# Revit family: Reece_Toilet_American Standard_Cygnet_Close Coupled Back to Wall_Bottom Inlet_With E Bidet
name_source: partatom
category: Plumbing Fixtures
revit_build: Autodesk Revit 2018 (Build: 20190510_1515(x64)
units: mm (PartAtom-declared; Revit-internal decimal feet)

## family parameters
Always vertical = Yes
Cut with Voids When Loaded = Yes
Part Type = Normal
Room Calculation Point = No
Round Connector Dimension = Use Diameter
Shared = No
Work Plane-Based = Yes

## types (1)
- Round_Soft Close_White
    Default Elevation = 0 mm  [stored 0 ft]
    Description = American Standard Cygnet Round Hygiene Rim Close Coupled Back to Wall Bottom Inlet Toilet Suite with SpaLet E-Bidet Seat White (4 Star)
    Disclaimer = THIS FILE IS THE PROPERTY OF THE REECE GROUP. IT MAY NOT BE REPRODUCED, REVERSE-ENGINEERED OR MODIFIED. ANY REPUBLICATION, TRANSMISSION OR DISTRIBUTION FOR THE PURPOSE OF COMMERCIALLY EXPLOITING THE FILES IS PROHIBITED.
    Keynote = Product #1805208, Reece_Toilet_American Standard_Cygnet_Close Coupled Back to Wall_Bottom Inlet_With E Bidet - Round_Soft Close_White
    Manufacturer = American Standard
    Model = Cygnet
    Reece_Back_Outlet_Offset = 190 mm  [stored 0.62336 ft]
    Reece_Bottom_Inlet = 12 mm  [stored 0.0393701 ft]
    Reece_Bottom_Outlet_Offset = 140 mm  [stored 0.459318 ft]
    Reece_Cistern = Reece_Toilet_American Standard_Cygnet_SpaLet_Round_Bottom Inlet_Cistern_Nested
    Reece_Cistern_Width = 375 mm  [stored 1.23031 ft]
    Reece_Detail_Additional = Close Coupled Back to Wall
    Reece_Detail_Connector = Bottom Inlet
    Reece_Detail_Disclaimer = THIS FILE IS THE PROPERTY OF THE REECE GROUP. IT MAY NOT BE REPRODUCED, REVERSE-ENGINEERED OR MODIFIED. ANY REPUBLICATION, TRANSMISSION OR DISTRIBUTION FOR THE PURPOSE OF COMMERCIALLY EXPLOITING THE FILES IS PROHIBITED.
    Reece_Detail_Function = P Trap / S Trap using conversion bend (supplied)
    Reece_Detail_Installation = Electrical input required. Refer to web page for further details.
    Reece_Detail_Shape = Round
    Reece_E Bidet_Inlet = 12 mm  [stored 0.0393701 ft]
    Reece_Material_Cistern = Reece_Vitreous China_White
    Reece_Material_Colour = Reece_Brass_Chrome
    Reece_Material_Main = Reece_Vitreous China_White
    Reece_Material_Seat = Reece_Plastic_White
    Reece_Material_Secondary = Reece_Brass_Chrome
    Reece_Overall_Height = 807 mm
    Reece_Overall_Projection = 680 mm  [stored 2.23097 ft]
    Reece_P_Trap = 102 mm
    Reece_Pan_Height = 400 mm  [stored 1.31234 ft]
    Reece_Pan_Width = 360 mm  [stored 1.1811 ft]
    Reece_Product_Brand = American Standard
    Reece_Product_Description = American Standard Cygnet Round Hygiene Rim Close Coupled Back to Wall Bottom Inlet Toilet Suite with SpaLet E-Bidet Seat White (4 Star)
    Reece_Product_Mount = Floor Mounted
    Reece_Product_Number = 1805208
    Reece_Product_Sub Brand = Cygnet
    Reece_Product_Web Page = https://www.reece.com.au
    Reece_S_Trap = 102 mm
    Reece_Toilet Seat = Reece_Toilet_American Standard_SpaLet_E Bidet_Toilet Seat_Nested
    Reece_Toilet Seat Cover = Reece_Toilet_American Standard_SpaLet_E Bidet_Seat Cover_Nested
    URL = https://www.reece.com.au

note: [stored X ft] marks values corroborated as IEEE doubles in the binary element streams (Revit-internal decimal feet)

## geometry (parser evidence)
native form markers: Sweep x7
no freeform markers — native parametric forms only
